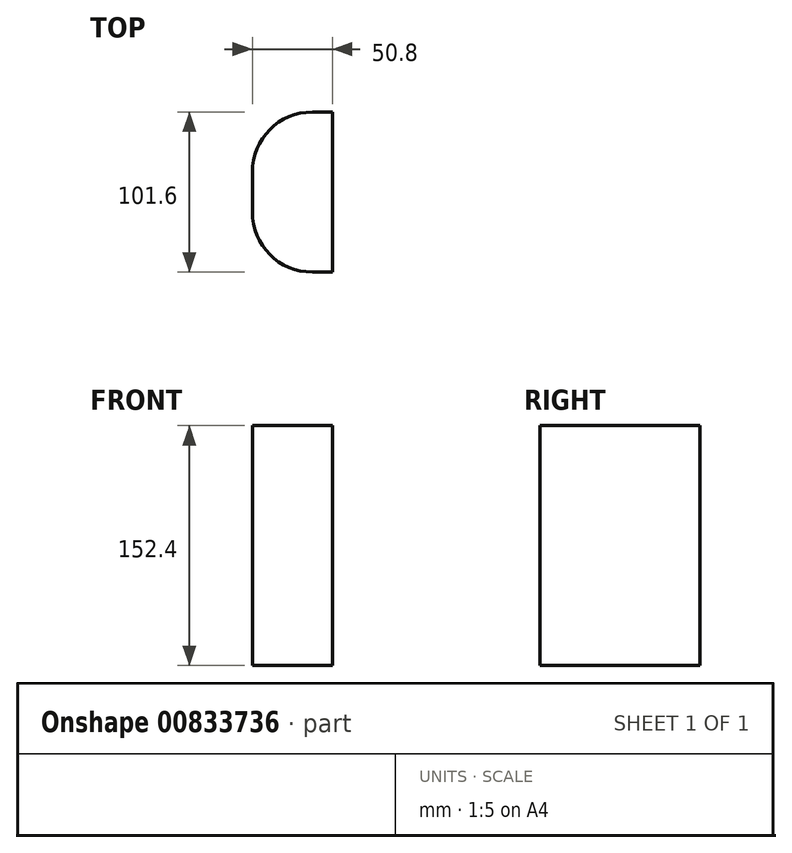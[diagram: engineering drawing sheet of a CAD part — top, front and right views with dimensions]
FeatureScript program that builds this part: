
annotation { "Feature Type Name" : "Feature", "Feature Type Description" : "" }
export const myFeature = defineFeature(function(context is Context, id is Id, definition is map)
    precondition{}
    {
        {
            var Q0;
            Q0=qCreatedBy(makeId("Top.planeOp"),FACE);
            var sketch = newSketch(context, id + "F0", { "sketchPlane" : qUnion([Q0])});
            skLineSegment(sketch, "E0.bottom", {"start": v(24.35, 32.35) * mm, "end": v(37.05, 32.35) * mm});
            skLineSegment(sketch, "E0.top", {"start": v(24.35, -69.25) * mm, "end": v(37.05, -69.25) * mm});
            skLineSegment(sketch, "E0.left", {"start": v(-13.75, -5.75) * mm, "end": v(-13.75, -31.15) * mm});
            skLineSegment(sketch, "E0.right", {"start": v(37.05, 32.35) * mm, "end": v(37.05, -69.25) * mm});
            skPoint(sketch, "E1.visualSharp", {"position": v(-13.75, 32.35) * mm});
            skArc(sketch, "E1.filletArc", {"start": v(24.35, 32.35) * mm, "mid": v(-2.59, 21.2) * mm, "end": v(-13.75, -5.75) * mm});
            skPoint(sketch, "E2.visualSharp", {"position": v(-13.75, -69.25) * mm});
            skArc(sketch, "E2.filletArc", {"start": v(-13.75, -31.15) * mm, "mid": v(-2.59, -58.09) * mm, "end": v(24.35, -69.25) * mm});
            skLineSegment(sketch, "E3", {"start": v(-13.75, -18.45) * mm, "end": v(37.05, -18.45) * mm});
            skSolve(sketch);
        }
        {
            var Q0;
            {var subQ2=sQuery(id+"F0.wireOp",EDGE,"E0.bottom");Q0=makeQuery(id+"F0.imprint","IMPRINT",FACE,{"disambiguationData":[TD([[makeQuery(id+"F0.imprint","IMPRINT",EDGE,{"derivedFrom":subQ2}),-1.0]])]});}
            var Q1;
            {var subQ2=sQuery(id+"F0.wireOp",EDGE,"E0.top");Q1=makeQuery(id+"F0.imprint","IMPRINT",FACE,{"disambiguationData":[TD([[makeQuery(id+"F0.imprint","IMPRINT",EDGE,{"derivedFrom":subQ2}),1.0]])]});}
            extrude(context, id + "F1", {"entities" : qUnion([Q0, Q1]), "depth" : 152.4 * mm, "offsetDistance" : 25.4 * mm});
        }
    });
